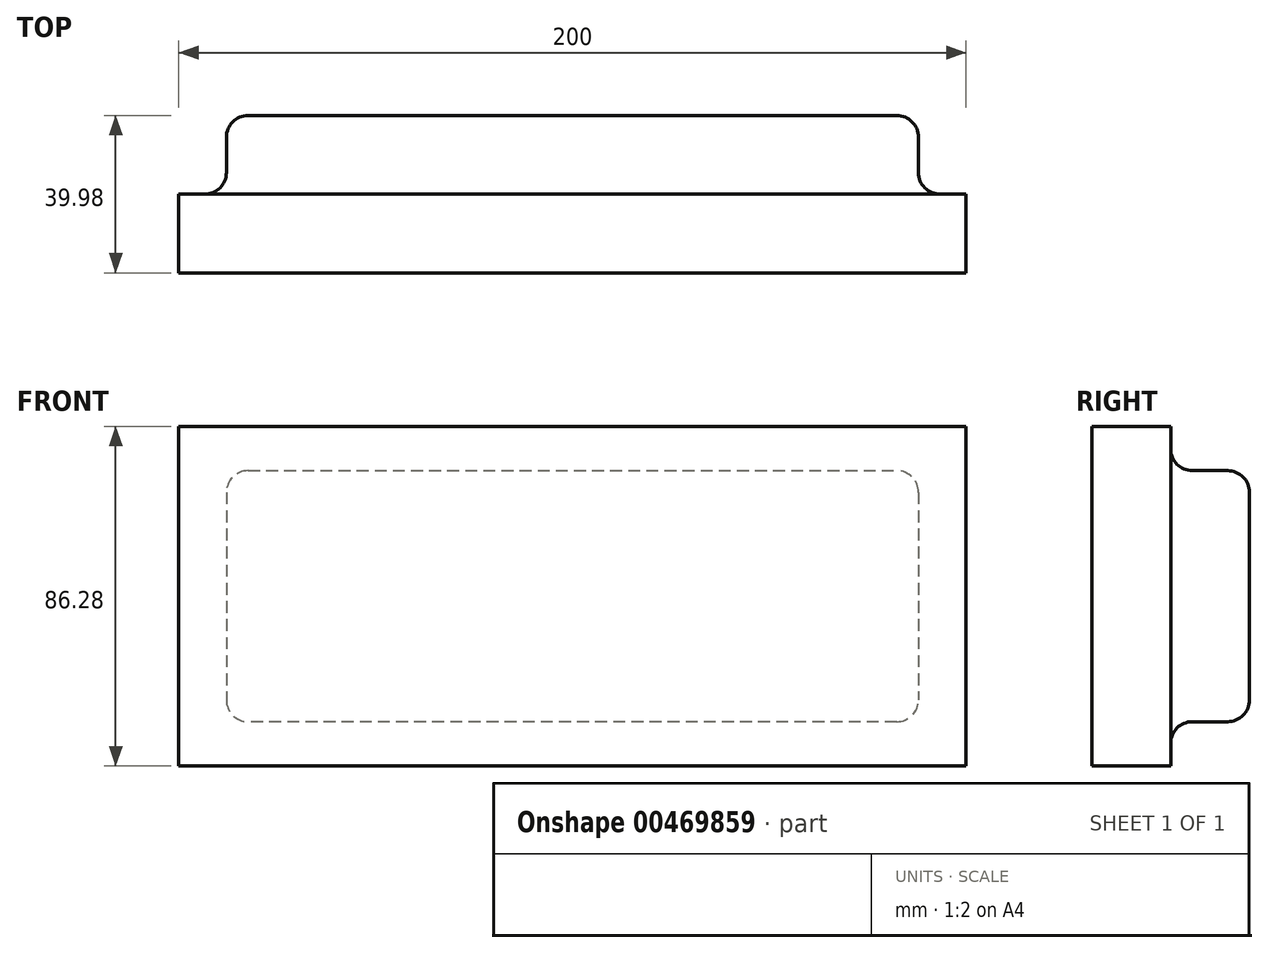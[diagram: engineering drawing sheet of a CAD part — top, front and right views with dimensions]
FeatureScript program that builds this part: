
annotation { "Feature Type Name" : "Feature", "Feature Type Description" : "" }
export const myFeature = defineFeature(function(context is Context, id is Id, definition is map)
    precondition{}
    {
        {
            var Q0;
            Q0=qCreatedBy(makeId("Front.planeOp"),FACE);
            var sketch = newSketch(context, id + "F0", { "sketchPlane" : qUnion([Q0])});
            skLineSegment(sketch, "E0.bottom", {"start": v(-72.62, 28.1) * mm, "end": v(127.38, 28.1) * mm});
            skLineSegment(sketch, "E0.top", {"start": v(-72.62, -58.18) * mm, "end": v(127.38, -58.18) * mm});
            skLineSegment(sketch, "E0.left", {"start": v(-72.62, 28.1) * mm, "end": v(-72.62, -58.18) * mm});
            skLineSegment(sketch, "E0.right", {"start": v(127.38, 28.1) * mm, "end": v(127.38, -58.18) * mm});
            skSolve(sketch);
        }
        {
            var Q0;
            Q0=makeQuery(id+"F0.imprint","IMPRINT",FACE,{"disambiguationData":[TD([[makeQuery(id+"F0.imprint","IMPRINT",EDGE,{"derivedFrom":sQuery(id+"F0.wireOp",EDGE,"E0.bottom")}),-1.0]])]});
            extrude(context, id + "F1", {"entities" : qUnion([Q0]), "depth" : 19.99 * mm});
        }
        {
            var Q0;
            Q0=makeQuery(id+"F1.opExtrude","CAP_FACE",FACE,{"disambiguationData":[OSD([sQuery(id+"F0.wireOp",EDGE,"E0.bottom"),sQuery(id+"F0.wireOp",EDGE,"E0.top"),sQuery(id+"F0.wireOp",EDGE,"E0.left"),sQuery(id+"F0.wireOp",EDGE,"E0.right")])],"isStart":true});
            var sketch = newSketch(context, id + "F2", { "sketchPlane" : qUnion([Q0])});
            skLineSegment(sketch, "E1", {"start": v(-115.3, 16.85) * mm, "end": v(-115.3, -46.93) * mm});
            skLineSegment(sketch, "E2", {"start": v(-115.3, -46.93) * mm, "end": v(60.54, -46.93) * mm});
            skLineSegment(sketch, "E3", {"start": v(60.54, 16.85) * mm, "end": v(60.54, -46.93) * mm});
            skLineSegment(sketch, "E4", {"start": v(60.54, 16.85) * mm, "end": v(-115.3, 16.85) * mm});
            skPoint(sketch, "E5.MirrorCS.start.orphan", {"position": v(-127.38, 28.1) * mm});
            skPoint(sketch, "E6.orphan", {"position": v(-127.38, -15.04) * mm});
            skPoint(sketch, "E7.MirrorCS.start.orphan", {"position": v(-127.38, -58.18) * mm});
            skPoint(sketch, "E8.trimOffspring.end.orphan", {"position": v(-27.38, -58.18) * mm});
            skPoint(sketch, "E9.start.orphan", {"position": v(-27.38, 28.1) * mm});
            skPoint(sketch, "E10.end.orphan", {"position": v(72.62, -15.04) * mm});
            skSolve(sketch);
        }
        {
            var Q0;
            Q0=makeQuery(id+"F2.imprint","IMPRINT",FACE,{"disambiguationData":[TD([[makeQuery(id+"F2.imprint","IMPRINT",EDGE,{"derivedFrom":sQuery(id+"F2.wireOp",EDGE,"E1")}),1.0]])]});
            extrude(context, id + "F3", {"entities" : qUnion([Q0]), "operationType" : NewBodyOperationType.ADD, "depth" : 19.99 * mm});
        }
        {
            var Q0;
            Q0=makeQuery(id+"F3.opExtrude","SWEPT_FACE",FACE,{"disambiguationData":[OSD([sQuery(id+"F2.wireOp",EDGE,"E4")])]});
            var Q1;
            Q1=makeQuery(id+"F3.opExtrude","SWEPT_FACE",FACE,{"disambiguationData":[OSD([sQuery(id+"F2.wireOp",EDGE,"E2")])]});
            var Q2;
            Q2=makeQuery(id+"F3.opExtrude","SWEPT_FACE",FACE,{"disambiguationData":[OSD([sQuery(id+"F2.wireOp",EDGE,"E3")])]});
            var Q3;
            Q3=makeQuery(id+"F3.opExtrude","SWEPT_FACE",FACE,{"disambiguationData":[OSD([sQuery(id+"F2.wireOp",EDGE,"E1")])]});
            fillet(context, id + "F4", {"entities" : qUnion([Q0, Q1, Q2, Q3]), "radius" : 5.52 * mm, "tangentPropagation" : true, "allowEdgeOverflow" : false});
        }
        {
            var Q0;
            Q0=makeQuery(id+"F3.opExtrude","CAP_FACE",FACE,{"disambiguationData":[OSD([sQuery(id+"F2.wireOp",EDGE,"E1"),sQuery(id+"F2.wireOp",EDGE,"E2"),sQuery(id+"F2.wireOp",EDGE,"E3"),sQuery(id+"F2.wireOp",EDGE,"E4")])],"isStart":false});
            var sketch = newSketch(context, id + "F5", { "sketchPlane" : qUnion([Q0])});
            skLineSegment(sketch, "E11", {"start": v(-109.78, -15.04) * mm, "end": v(55.02, -15.04) * mm});
            skSolve(sketch);
        }
        {
            var Q0;
            Q0=sQuery(id+"F5.wireOp",EDGE,"E11");
            extrude(context, id + "F6", {"bodyType" : ToolBodyType.SURFACE, "surfaceEntities" : qUnion([Q0]), "depth" : 147.07 * mm});
        }
    });
